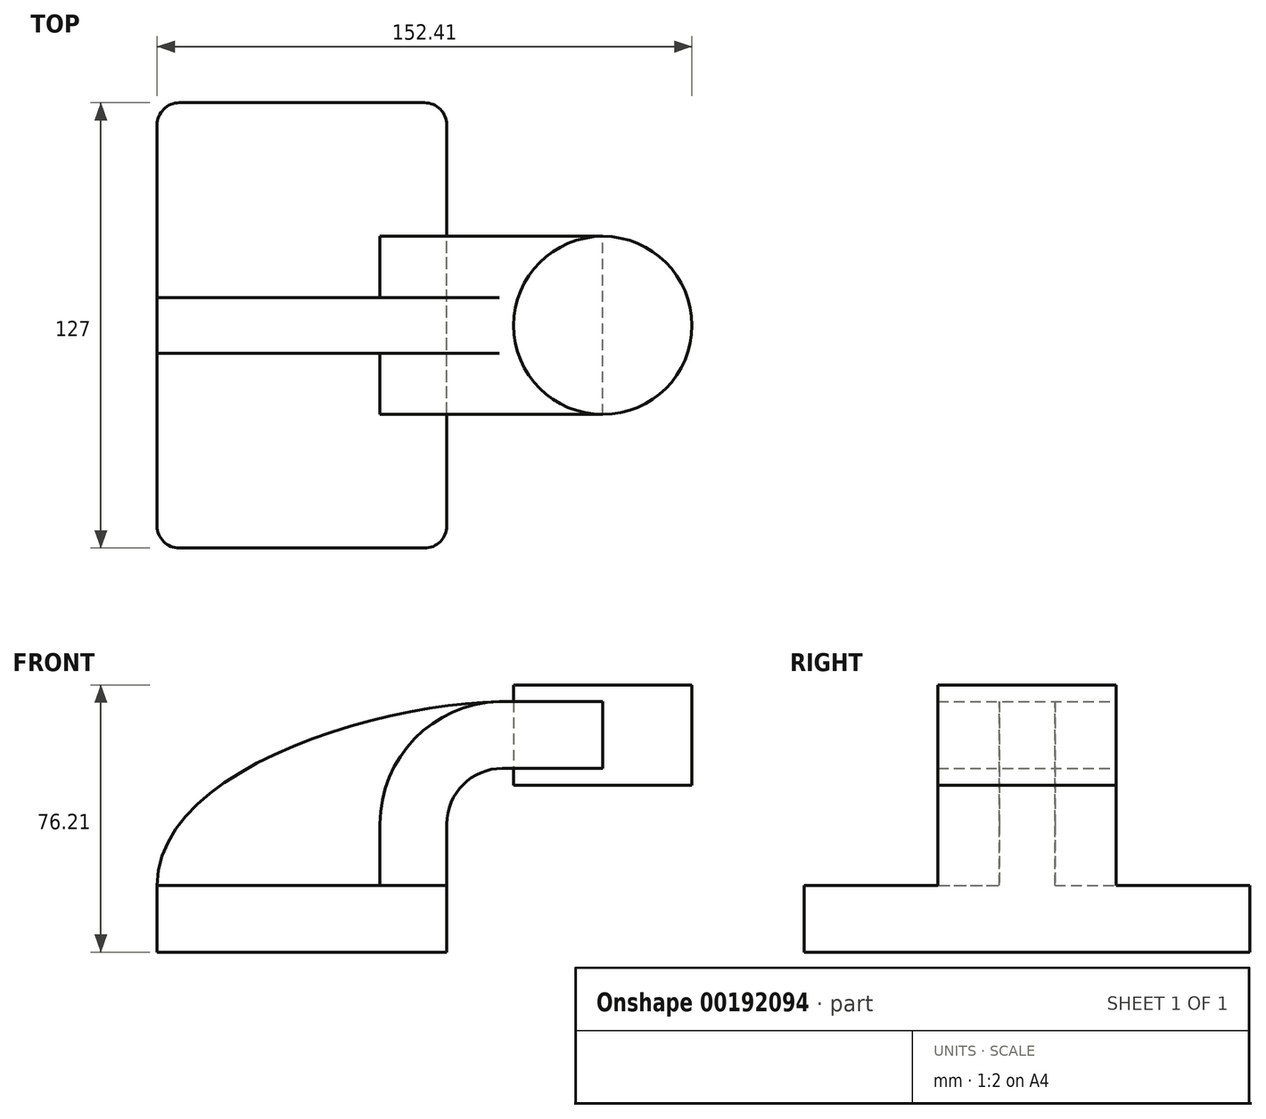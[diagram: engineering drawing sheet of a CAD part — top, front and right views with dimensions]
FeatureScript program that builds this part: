
annotation { "Feature Type Name" : "Feature", "Feature Type Description" : "" }
export const myFeature = defineFeature(function(context is Context, id is Id, definition is map)
    precondition{}
    {
        {
            var Q0;
            Q0=qCreatedBy(makeId("Front.planeOp"),FACE);
            var sketch = newSketch(context, id + "F0", { "sketchPlane" : qUnion([Q0])});
            skLineSegment(sketch, "E0.bottom", {"start": v(-41.27, -9.52) * mm, "end": v(41.28, -9.52) * mm});
            skLineSegment(sketch, "E0.top", {"start": v(-41.28, 9.53) * mm, "end": v(41.28, 9.53) * mm});
            skLineSegment(sketch, "E0.left", {"start": v(-41.28, -9.52) * mm, "end": v(-41.28, 9.53) * mm});
            skLineSegment(sketch, "E0.right", {"start": v(41.27, -9.52) * mm, "end": v(41.27, 9.53) * mm});
            skPoint(sketch, "E0.middle", {"position": v(0, 0) * mm});
            skLineSegment(sketch, "E1.bottom", {"start": v(111.12, 38.1) * mm, "end": v(60.32, 38.1) * mm});
            skLineSegment(sketch, "E1.top", {"start": v(111.12, 66.68) * mm, "end": v(60.32, 66.68) * mm});
            skLineSegment(sketch, "E1.left", {"start": v(111.12, 38.1) * mm, "end": v(111.12, 66.68) * mm});
            skLineSegment(sketch, "E1.right", {"start": v(60.32, 38.1) * mm, "end": v(60.32, 66.68) * mm});
            skPoint(sketch, "E1.middle", {"position": v(85.72, 52.39) * mm});
            skLineSegment(sketch, "E2", {"start": v(41.27, 27) * mm, "end": v(41.27, 9.53) * mm});
            skArc(sketch, "E3", {"start": v(41.27, 27) * mm, "mid": v(45.92, 38.23) * mm, "end": v(57.15, 42.88) * mm});
            skLineSegment(sketch, "E4", {"start": v(57.15, 42.88) * mm, "end": v(57.15, 42.88) * mm});
            skLineSegment(sketch, "E5", {"start": v(57.15, 42.88) * mm, "end": v(85.72, 42.88) * mm});
            skLineSegment(sketch, "E6.0", {"start": v(22.22, 27) * mm, "end": v(22.22, 9.53) * mm});
            skArc(sketch, "E6.1", {"start": v(22.22, 27) * mm, "mid": v(32.45, 51.7) * mm, "end": v(57.15, 61.93) * mm});
            skLineSegment(sketch, "E6.2", {"start": v(57.15, 61.93) * mm, "end": v(85.72, 61.93) * mm});
            skLineSegment(sketch, "E7", {"start": v(85.72, 38.1) * mm, "end": v(85.72, 66.68) * mm});
            skFitSpline(sketch, "E8", {"points": [v(-41.28, 9.53) * mm, v(57.15, 61.93) * mm], "startDerivative": vector(0.64, 101.12) * mm, "endDerivative": vector(101.52, 0.9) * mm});
            skSolve(sketch);
        }
        {
            var Q0;
            {var subQ5=sQuery(id+"F0.wireOp",EDGE,"E2");Q0=makeQuery(id+"F0.imprint","IMPRINT",FACE,{"disambiguationData":[TD([[makeQuery(id+"F0.imprint","IMPRINT",EDGE,{"derivedFrom":subQ5}),-1.0]])]});}
            var Q1;
            {var subQ0=sQuery(id+"F0.wireOp",EDGE,"E5");var subQ1=sQuery(id+"F0.wireOp",EDGE,"E1.right");var subQ2=makeQuery(id+"F0.imprint","INTERSECT",VERTEX,{"derivedFrom":[subQ1,subQ0]});Q1=makeQuery(id+"F0.imprint","IMPRINT",FACE,{"disambiguationData":[TD([[makeQuery(id+"F0.imprint","IMPRINT",EDGE,{"disambiguationData":[TD([[subQ2,-1.0]])],"derivedFrom":subQ1}),-1.0]])]});}
            extrude(context, id + "F1", {"entities" : qUnion([Q0, Q1]), "endBound" : BoundingType.SYMMETRIC, "depth" : 50.8 * mm});
        }
        {
            var Q0;
            Q0=makeQuery(id+"F0.imprint","IMPRINT",FACE,{"disambiguationData":[TD([[makeQuery(id+"F0.imprint","IMPRINT",EDGE,{"derivedFrom":sQuery(id+"F0.wireOp",EDGE,"E0.bottom")}),1.0]])]});
            extrude(context, id + "F2", {"entities" : qUnion([Q0]), "operationType" : NewBodyOperationType.ADD, "endBound" : BoundingType.SYMMETRIC, "depth" : 127 * mm});
        }
        {
            var Q0;
            {var subQ3=sQuery(id+"F0.wireOp",EDGE,"E6.0");Q0=makeQuery(id+"F0.imprint","IMPRINT",FACE,{"disambiguationData":[TD([[makeQuery(id+"F0.imprint","IMPRINT",EDGE,{"derivedFrom":subQ3}),-1.0]])]});}
            extrude(context, id + "F3", {"entities" : qUnion([Q0]), "operationType" : NewBodyOperationType.ADD, "endBound" : BoundingType.SYMMETRIC, "depth" : 15.88 * mm});
        }
        {
            var Q0;
            Q0=makeQuery(id+"F2.opExtrude","CAP_EDGE",EDGE,{"disambiguationData":[OSD([sQuery(id+"F0.wireOp",EDGE,"E0.left")])],"isStart":false});
            var Q1;
            Q1=makeQuery(id+"F2.opExtrude","CAP_EDGE",EDGE,{"disambiguationData":[OSD([sQuery(id+"F0.wireOp",EDGE,"E0.right")])],"isStart":false});
            var Q2;
            Q2=makeQuery(id+"F2.opExtrude","CAP_EDGE",EDGE,{"disambiguationData":[OSD([sQuery(id+"F0.wireOp",EDGE,"E0.right")])],"isStart":true});
            var Q3;
            Q3=makeQuery(id+"F2.opExtrude","CAP_EDGE",EDGE,{"disambiguationData":[OSD([sQuery(id+"F0.wireOp",EDGE,"E0.left")])],"isStart":true});
            fillet(context, id + "F4", {"entities" : qUnion([Q0, Q1, Q2, Q3]), "radius" : 6.35 * mm, "tangentPropagation" : true, "allowEdgeOverflow" : false});
        }
        {
            var Q0;
            {var subQ0=sQuery(id+"F0.wireOp",EDGE,"E1.left");Q0=makeQuery(id+"F0.imprint","IMPRINT",FACE,{"disambiguationData":[TD([[makeQuery(id+"F0.imprint","IMPRINT",EDGE,{"derivedFrom":subQ0}),1.0]])]});}
            var Q1;
            Q1=sQuery(id+"F0.wireOp",EDGE,"E7");
            revolve(context, id + "F5", {"entities" : qUnion([Q0]), "axis" : qUnion([Q1]), "revolveType" : RevolveType.FULL});
        }
    });
